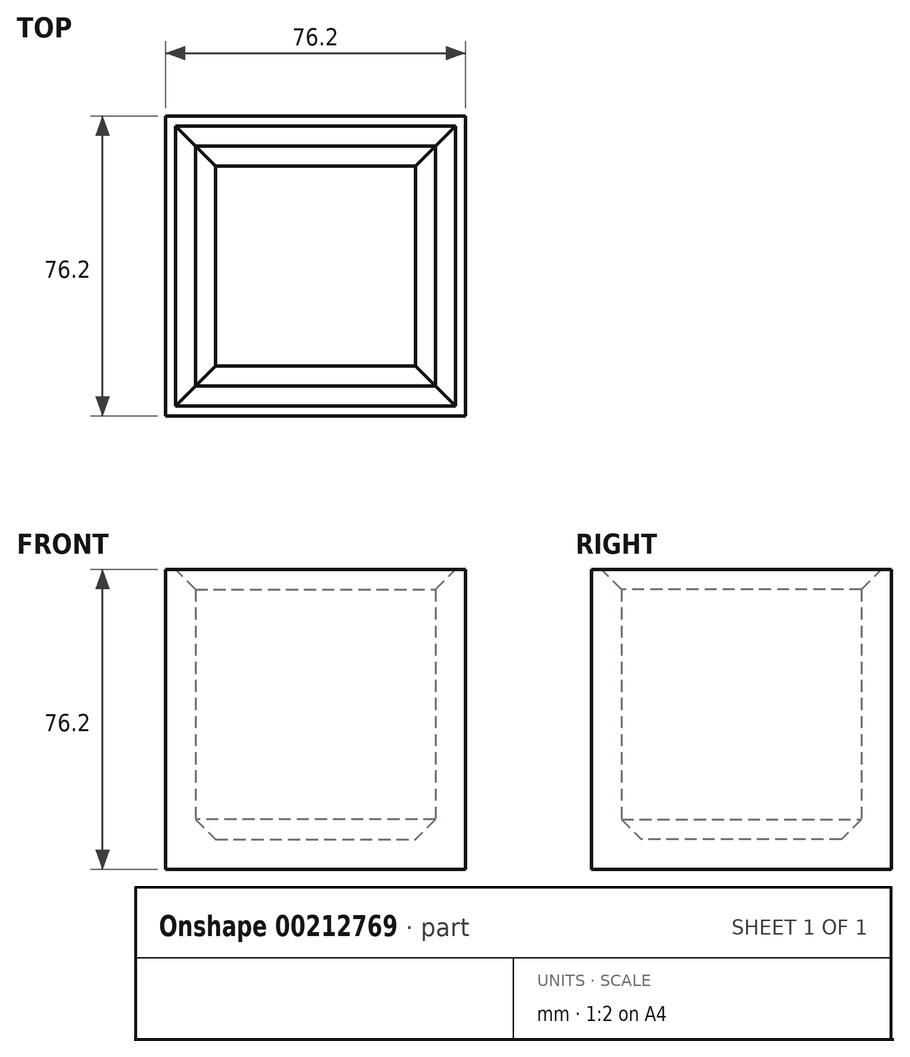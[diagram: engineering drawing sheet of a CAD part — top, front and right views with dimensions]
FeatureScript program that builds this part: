
annotation { "Feature Type Name" : "Feature", "Feature Type Description" : "" }
export const myFeature = defineFeature(function(context is Context, id is Id, definition is map)
    precondition{}
    {
        {
            var Q0;
            Q0=qCreatedBy(makeId("Front.planeOp"),FACE);
            var sketch = newSketch(context, id + "F0", { "sketchPlane" : qUnion([Q0])});
            skLineSegment(sketch, "E0.bottom", {"start": v(-38.1, 38.1) * mm, "end": v(38.1, 38.1) * mm});
            skLineSegment(sketch, "E0.top", {"start": v(-38.1, -38.1) * mm, "end": v(38.1, -38.1) * mm});
            skLineSegment(sketch, "E0.left", {"start": v(-38.1, 38.1) * mm, "end": v(-38.1, -38.1) * mm});
            skLineSegment(sketch, "E0.right", {"start": v(38.1, 38.1) * mm, "end": v(38.1, -38.1) * mm});
            skPoint(sketch, "E0.middle", {"position": v(0, 0) * mm});
            skSolve(sketch);
        }
        {
            var Q0;
            Q0=makeQuery(id+"F0.imprint","IMPRINT",FACE,{"disambiguationData":[TD([[makeQuery(id+"F0.imprint","IMPRINT",EDGE,{"derivedFrom":sQuery(id+"F0.wireOp",EDGE,"E0.bottom")}),-1.0]])]});
            extrude(context, id + "F1", {"entities" : qUnion([Q0]), "depth" : 38.1 * mm});
        }
        {
            var Q0;
            Q0=makeQuery(id+"F1.opExtrude","CAP_FACE",FACE,{"disambiguationData":[OSD([sQuery(id+"F0.wireOp",EDGE,"E0.bottom"),sQuery(id+"F0.wireOp",EDGE,"E0.top"),sQuery(id+"F0.wireOp",EDGE,"E0.left"),sQuery(id+"F0.wireOp",EDGE,"E0.right")])],"isStart":true});
            extrude(context, id + "F2", {"entities" : qUnion([Q0]), "operationType" : NewBodyOperationType.ADD, "depth" : 38.1 * mm});
        }
        {
            var Q0;
            {var subQ0=sQuery(id+"F0.wireOp",EDGE,"E0.bottom");Q0=makeQuery(id+"F2.boolean.opBoolean","MERGE",FACE,{"derivedFrom":[makeQuery(id+"F1.opExtrude","SWEPT_FACE",FACE,{"disambiguationData":[OSD([subQ0])]}),makeQuery(id+"F2.opExtrude","SWEPT_FACE",FACE,{"disambiguationData":[OSD([subQ0])]})]});}
            shell(context, id + "F3", {"entities" : qUnion([Q0]), "thickness" : 7.62 * mm});
        }
        {
            var Q0;
            Q0=makeQuery(id+"F3.opShell","OFFSET_EDGE",EDGE,{"disambiguationData":[OSD([sQuery(id+"F0.wireOp",EDGE,"E0.bottom"),sQuery(id+"F0.wireOp",EDGE,"E0.left")])]});
            var Q1;
            {var subQ0=sQuery(id+"F0.wireOp",EDGE,"E0.bottom");Q1=makeQuery(id+"F3.opShell","OFFSET_EDGE",EDGE,{"disambiguationData":[OSD([subQ0]),TDD([makeQuery(id+"F1.opExtrude","CAP_EDGE",EDGE,{"disambiguationData":[OSD([subQ0])],"isStart":false})])]});}
            var Q2;
            {var subQ0=sQuery(id+"F0.wireOp",EDGE,"E0.bottom");Q2=makeQuery(id+"F3.opShell","OFFSET_EDGE",EDGE,{"disambiguationData":[OSD([subQ0]),TDD([makeQuery(id+"F2.opExtrude","CAP_EDGE",EDGE,{"disambiguationData":[OSD([subQ0])],"isStart":false})])]});}
            var Q3;
            Q3=makeQuery(id+"F3.opShell","OFFSET_EDGE",EDGE,{"disambiguationData":[OSD([sQuery(id+"F0.wireOp",EDGE,"E0.bottom"),sQuery(id+"F0.wireOp",EDGE,"E0.right")])]});
            chamfer(context, id + "F4", {"entities" : qUnion([Q0, Q1, Q2, Q3]), "width" : 5.08 * mm, "tangentPropagation" : true});
        }
        {
            var Q0;
            {var subQ0=sQuery(id+"F0.wireOp",EDGE,"E0.top");Q0=makeQuery(id+"F3.opShell","OFFSET_EDGE",EDGE,{"disambiguationData":[OSD([subQ0]),TDD([makeQuery(id+"F2.opExtrude","CAP_EDGE",EDGE,{"disambiguationData":[OSD([subQ0])],"isStart":false})])]});}
            var Q1;
            Q1=makeQuery(id+"F3.opShell","OFFSET_EDGE",EDGE,{"disambiguationData":[OSD([sQuery(id+"F0.wireOp",EDGE,"E0.top"),sQuery(id+"F0.wireOp",EDGE,"E0.left")])]});
            var Q2;
            Q2=makeQuery(id+"F3.opShell","OFFSET_EDGE",EDGE,{"disambiguationData":[OSD([sQuery(id+"F0.wireOp",EDGE,"E0.top"),sQuery(id+"F0.wireOp",EDGE,"E0.right")])]});
            var Q3;
            {var subQ0=sQuery(id+"F0.wireOp",EDGE,"E0.top");Q3=makeQuery(id+"F3.opShell","OFFSET_EDGE",EDGE,{"disambiguationData":[OSD([subQ0]),TDD([makeQuery(id+"F1.opExtrude","CAP_EDGE",EDGE,{"disambiguationData":[OSD([subQ0])],"isStart":false})])]});}
            chamfer(context, id + "F5", {"entities" : qUnion([Q0, Q1, Q2, Q3]), "width" : 5.08 * mm, "tangentPropagation" : true});
        }
    });
